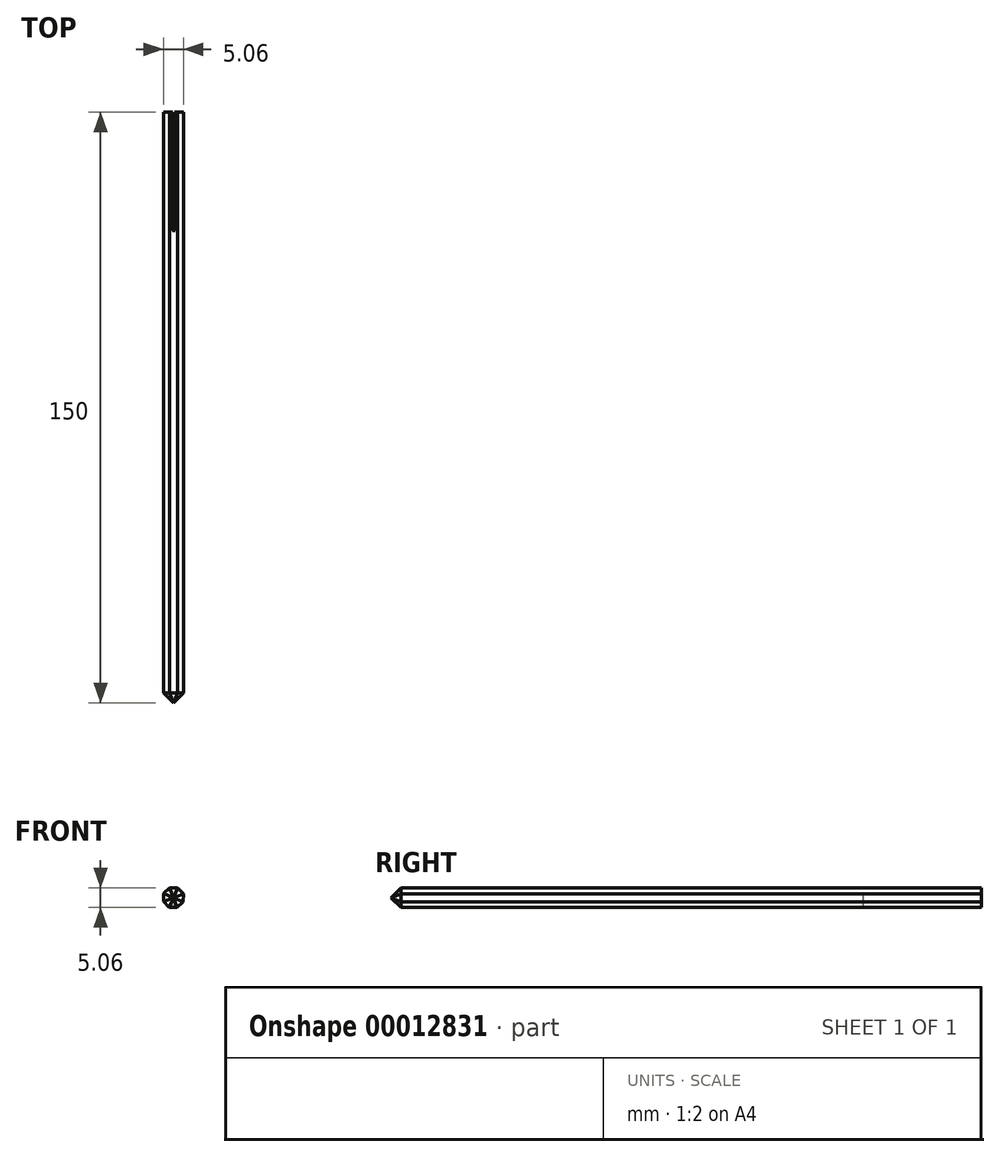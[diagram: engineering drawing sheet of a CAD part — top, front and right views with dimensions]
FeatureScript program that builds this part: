
annotation { "Feature Type Name" : "Feature", "Feature Type Description" : "" }
export const myFeature = defineFeature(function(context is Context, id is Id, definition is map)
    precondition{}
    {
        {
            var Q0;
            Q0=qCreatedBy(makeId("Front.planeOp"),FACE);
            var sketch = newSketch(context, id + "F0", { "sketchPlane" : qUnion([Q0])});
            skCircle(sketch, "E0", {"center": v(0, 0) * mm, "radius": 2.5 * mm});
            skCircle(sketch, "E1.cCircle", {"center": v(0, 0) * mm, "radius": 2.5 * mm, "construction": true});
            skLineSegment(sketch, "E1.0", {"start": v(-2.47, 1.1) * mm, "end": v(-0.97, 2.53) * mm});
            skLineSegment(sketch, "E1.1", {"start": v(-0.97, 2.53) * mm, "end": v(1.1, 2.47) * mm});
            skLineSegment(sketch, "E1.2", {"start": v(1.1, 2.47) * mm, "end": v(2.53, 0.97) * mm});
            skLineSegment(sketch, "E1.3", {"start": v(2.53, 0.97) * mm, "end": v(2.47, -1.1) * mm});
            skLineSegment(sketch, "E1.4", {"start": v(2.47, -1.1) * mm, "end": v(0.97, -2.53) * mm});
            skLineSegment(sketch, "E1.5", {"start": v(0.97, -2.53) * mm, "end": v(-1.1, -2.47) * mm});
            skLineSegment(sketch, "E1.6", {"start": v(-1.1, -2.47) * mm, "end": v(-2.53, -0.97) * mm});
            skLineSegment(sketch, "E1.7", {"start": v(-2.53, -0.97) * mm, "end": v(-2.47, 1.1) * mm});
            skPoint(sketch, "E1.0.midPoint", {"position": v(-1.72, 1.82) * mm});
            skSolve(sketch);
        }
        {
            var Q0;
            {var subQ0=sQuery(id+"F0.wireOp",EDGE,"E0");var subQ7=makeQuery(id+"F0.imprint","INTERSECT",VERTEX,{"derivedFrom":[subQ0,sQuery(id+"F0.wireOp",EDGE,"E1.1")]});Q0=makeQuery(id+"F0.imprint","IMPRINT",FACE,{"disambiguationData":[TD([[makeQuery(id+"F0.imprint","IMPRINT",EDGE,{"disambiguationData":[TD([[subQ7,1.0]])],"derivedFrom":subQ0}),1.0]])]});}
            var Q1;
            {var subQ0=sQuery(id+"F0.wireOp",EDGE,"E1.1");var subQ1=sQuery(id+"F0.wireOp",EDGE,"E0");var subQ2=makeQuery(id+"F0.imprint","INTERSECT",VERTEX,{"derivedFrom":[subQ1,subQ0]});Q1=makeQuery(id+"F0.imprint","IMPRINT",FACE,{"disambiguationData":[TD([[makeQuery(id+"F0.imprint","IMPRINT",EDGE,{"disambiguationData":[TD([[subQ2,-1.0]])],"derivedFrom":subQ1}),-1.0]])]});}
            var Q2;
            {var subQ1=sQuery(id+"F0.wireOp",EDGE,"E0");var subQ3=sQuery(id+"F0.wireOp",EDGE,"E1.0");var subQ5=makeQuery(id+"F0.imprint","INTERSECT",VERTEX,{"derivedFrom":[subQ1,subQ3]});Q2=makeQuery(id+"F0.imprint","IMPRINT",FACE,{"disambiguationData":[TD([[makeQuery(id+"F0.imprint","IMPRINT",EDGE,{"disambiguationData":[TD([[subQ5,-1.0]])],"derivedFrom":subQ1}),-1.0]])]});}
            var Q3;
            {var subQ0=sQuery(id+"F0.wireOp",EDGE,"E1.7");var subQ1=sQuery(id+"F0.wireOp",EDGE,"E0");var subQ2=makeQuery(id+"F0.imprint","INTERSECT",VERTEX,{"derivedFrom":[subQ1,subQ0]});Q3=makeQuery(id+"F0.imprint","IMPRINT",FACE,{"disambiguationData":[TD([[makeQuery(id+"F0.imprint","IMPRINT",EDGE,{"disambiguationData":[TD([[subQ2,-1.0]])],"derivedFrom":subQ1}),-1.0]])]});}
            var Q4;
            {var subQ0=sQuery(id+"F0.wireOp",EDGE,"E1.6");var subQ1=sQuery(id+"F0.wireOp",EDGE,"E0");var subQ2=makeQuery(id+"F0.imprint","INTERSECT",VERTEX,{"derivedFrom":[subQ1,subQ0]});Q4=makeQuery(id+"F0.imprint","IMPRINT",FACE,{"disambiguationData":[TD([[makeQuery(id+"F0.imprint","IMPRINT",EDGE,{"disambiguationData":[TD([[subQ2,-1.0]])],"derivedFrom":subQ1}),-1.0]])]});}
            var Q5;
            {var subQ1=sQuery(id+"F0.wireOp",EDGE,"E0");var subQ3=sQuery(id+"F0.wireOp",EDGE,"E1.1");var subQ5=makeQuery(id+"F0.imprint","INTERSECT",VERTEX,{"derivedFrom":[subQ1,subQ3]});Q5=makeQuery(id+"F0.imprint","IMPRINT",FACE,{"disambiguationData":[TD([[makeQuery(id+"F0.imprint","IMPRINT",EDGE,{"disambiguationData":[TD([[subQ5,1.0]])],"derivedFrom":subQ1}),-1.0]])]});}
            var Q6;
            {var subQ1=sQuery(id+"F0.wireOp",EDGE,"E0");var subQ3=sQuery(id+"F0.wireOp",EDGE,"E1.2");var subQ5=makeQuery(id+"F0.imprint","INTERSECT",VERTEX,{"derivedFrom":[subQ1,subQ3]});Q6=makeQuery(id+"F0.imprint","IMPRINT",FACE,{"disambiguationData":[TD([[makeQuery(id+"F0.imprint","IMPRINT",EDGE,{"disambiguationData":[TD([[subQ5,1.0]])],"derivedFrom":subQ1}),-1.0]])]});}
            var Q7;
            {var subQ0=sQuery(id+"F0.wireOp",EDGE,"E1.4");var subQ1=sQuery(id+"F0.wireOp",EDGE,"E0");var subQ2=makeQuery(id+"F0.imprint","INTERSECT",VERTEX,{"derivedFrom":[subQ1,subQ0]});Q7=makeQuery(id+"F0.imprint","IMPRINT",FACE,{"disambiguationData":[TD([[makeQuery(id+"F0.imprint","IMPRINT",EDGE,{"disambiguationData":[TD([[subQ2,-1.0]])],"derivedFrom":subQ1}),-1.0]])]});}
            var Q8;
            {var subQ0=sQuery(id+"F0.wireOp",EDGE,"E1.5");var subQ1=sQuery(id+"F0.wireOp",EDGE,"E0");var subQ2=makeQuery(id+"F0.imprint","INTERSECT",VERTEX,{"derivedFrom":[subQ1,subQ0]});Q8=makeQuery(id+"F0.imprint","IMPRINT",FACE,{"disambiguationData":[TD([[makeQuery(id+"F0.imprint","IMPRINT",EDGE,{"disambiguationData":[TD([[subQ2,-1.0]])],"derivedFrom":subQ1}),-1.0]])]});}
            extrude(context, id + "F1", {"entities" : qUnion([Q0, Q1, Q2, Q3, Q4, Q5, Q6, Q7, Q8]), "depth" : 150 * mm});
        }
        {
            var Q0;
            Q0=makeQuery(id+"F1.opExtrude","SWEPT_FACE",FACE,{"disambiguationData":[OSD([sQuery(id+"F0.wireOp",EDGE,"E1.1")])]});
            var sketch = newSketch(context, id + "F2", { "sketchPlane" : qUnion([Q0])});
            skLineSegment(sketch, "E2", {"start": v(-0.3, 0) * mm, "end": v(-0.3, -30) * mm});
            skLineSegment(sketch, "E3", {"start": v(-0.3, -30) * mm, "end": v(0, -30) * mm});
            skLineSegment(sketch, "E4", {"start": v(0, -30) * mm, "end": v(0, 0) * mm});
            skLineSegment(sketch, "E5", {"start": v(0, 0) * mm, "end": v(-0.3, 0) * mm});
            skLineSegment(sketch, "E6.0.MirrorCS", {"start": v(0.3, -30) * mm, "end": v(0, -30) * mm});
            skLineSegment(sketch, "E7.0.MirrorCS", {"start": v(0.3, 0) * mm, "end": v(0.3, -30) * mm});
            skLineSegment(sketch, "E8.0.MirrorCS", {"start": v(0, 0) * mm, "end": v(0.3, 0) * mm});
            skSolve(sketch);
        }
        {
            var Q0;
            {var subQ5=sQuery(id+"F2.wireOp",EDGE,"E4");Q0=makeQuery(id+"F2.imprint","IMPRINT",FACE,{"disambiguationData":[TD([[makeQuery(id+"F2.imprint","IMPRINT",EDGE,{"derivedFrom":subQ5}),1.0]])]});}
            var Q1;
            {var subQ5=sQuery(id+"F2.wireOp",EDGE,"E4");Q1=makeQuery(id+"F2.imprint","IMPRINT",FACE,{"disambiguationData":[TD([[makeQuery(id+"F2.imprint","IMPRINT",EDGE,{"derivedFrom":subQ5}),-1.0]])]});}
            extrude(context, id + "F3", {"entities" : qUnion([Q0, Q1]), "operationType" : NewBodyOperationType.REMOVE, "endBound" : BoundingType.THROUGH_ALL, "oppositeDirection" : true, "depth" : 25.4 * mm});
        }
        {
            var Q0;
            Q0=makeQuery(id+"F1.opExtrude","CAP_EDGE",EDGE,{"disambiguationData":[OSD([sQuery(id+"F0.wireOp",EDGE,"E1.1")])],"isStart":false});
            var Q1;
            Q1=makeQuery(id+"F1.opExtrude","CAP_EDGE",EDGE,{"disambiguationData":[OSD([sQuery(id+"F0.wireOp",EDGE,"E1.2")])],"isStart":false});
            var Q2;
            Q2=makeQuery(id+"F1.opExtrude","CAP_EDGE",EDGE,{"disambiguationData":[OSD([sQuery(id+"F0.wireOp",EDGE,"E1.3")])],"isStart":false});
            var Q3;
            Q3=makeQuery(id+"F1.opExtrude","CAP_EDGE",EDGE,{"disambiguationData":[OSD([sQuery(id+"F0.wireOp",EDGE,"E1.4")])],"isStart":false});
            var Q4;
            Q4=makeQuery(id+"F1.opExtrude","CAP_EDGE",EDGE,{"disambiguationData":[OSD([sQuery(id+"F0.wireOp",EDGE,"E1.5")])],"isStart":false});
            var Q5;
            Q5=makeQuery(id+"F1.opExtrude","CAP_EDGE",EDGE,{"disambiguationData":[OSD([sQuery(id+"F0.wireOp",EDGE,"E1.6")])],"isStart":false});
            var Q6;
            Q6=makeQuery(id+"F1.opExtrude","CAP_EDGE",EDGE,{"disambiguationData":[OSD([sQuery(id+"F0.wireOp",EDGE,"E1.7")])],"isStart":false});
            var Q7;
            Q7=makeQuery(id+"F1.opExtrude","CAP_EDGE",EDGE,{"disambiguationData":[OSD([sQuery(id+"F0.wireOp",EDGE,"E1.0")])],"isStart":false});
            chamfer(context, id + "F4", {"entities" : qUnion([Q0, Q1, Q2, Q3, Q4, Q5, Q6, Q7]), "width" : 2.5 * mm, "tangentPropagation" : true});
        }
    });
